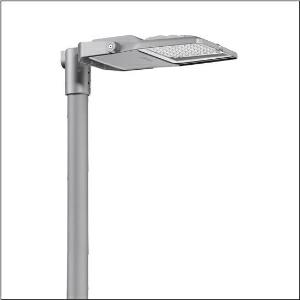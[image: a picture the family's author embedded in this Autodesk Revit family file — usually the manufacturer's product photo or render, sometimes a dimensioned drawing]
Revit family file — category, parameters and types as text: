
# Revit family: floodlight_fl_21_iq_mini___pl33t_5xa7772d4f3a_7ca2
name_source: partatom
category: Lighting Fixtures
units: mm (PartAtom-declared; Revit-internal decimal feet)

## family parameters
Cut with Voids When Loaded = No
Host = Face
Light Source = No
Part Type = Normal
Room Calculation Point = No
Round Connector Dimension = Use Diameter
Shared = No

## types (1)
- --- (1 x LED, 18390 lm, 143 W, 4000K)
    Apparent Load = 143 VA
    CIE Flux Codes = 26 75 99 100 100
    Color Rendering = 70
    Color Temperature = 4000K
    Default Elevation = 1800 mm
    Description = Floodlight FL 21 iQ mini, floodlight, primary light control with lens, of PMMA, primary optical cover: protective disc, of toughened safety glass, transparent, light distribution: PL33T, light emission: direct distribution, installation type: surface-mounted, LED, High Power LED, rated luminous flux: 18.390lm, luminous efficacy: 129lm/W, light colour: 740, colour temperature: 4000K, control: Auto-Match, Temp-Guard, Night-Set, Smart-Wire, Desk-Remote (wireless, voltage-free reading and setting of iQ features in the workshop via application-optimized NFC function/RFID function), optimised constant luminous flux control (CLO 2.0), Light-Fading, Lumen-Switch, with terminal, 6-pole, mains connection: 220..240V, AC, 50/60Hz, start of lifetime: 143W, end of service life: 152W, reduction: 61W, luminaire housing, of diecast aluminium, powder-coated, Siteco® metallic grey (DB 702S), corrosivity category C5 mid according to DIN EN ISO 12944, sealing non-destructively replaceable, please order mast flange separately, mast bracket, of steel, galvanised, powder-coated, protection rating (complete): IP66, insulation class (complete): insulation class II (safety insulation), certification: CE, ENEC, VDE, protection symbol: D, impact resistance: IK08, permissible operating ambient temperature: -40..+40°C, permissible operating ambient temperature for outdoor applications: -40..+50°C, standard: DIN EN 12944, LABS conformity tested according to VDMA 24364:2018-05, packaging unit: 1 piece

Light Distribution: PL33T
    Height = 70 mm
    Lamp = 1 x LED
    Lamp Light Flux = 18390 lm
    Lamp Power = 143 W
    Lamp count = 1
    Length = 485 mm
    Luminous efficacy = 129 lm/W
    Manufacturer = Siteco
    ModVariant = No
    Model = 5XA7772D4F3A
    Number of Poles = 1
    OnlyDefault = Yes
    Power Factor = 1
    Product Name = Floodlight FL 21 iQ mini | PL33T
    Product group = floodlight | pylon annexe
    ProductGroupID = 6200
    Protection Class = Protection class II
    Protection Degree = IP 66
    RLX_Detail_Level = 1
    RLX_Emergency_Light_Flux = 0 lm
    RLX_Emergency_Type = 0
    RLX_Emergency_Type_DB = No
    RlxData = <blob elided: 101605 chars, md5=edd52d3b>
    Socket = socket
    Standby Power = 0 W
    System Light Flux = 18390 lm
    System Power = 143 W
    Type Comments = factory setting: luminous flux: 100 % | dim-lin: 254 | 730 mA
    Type Image = l_1007125.jpg
    URL = http://relux.com
    VarID = @adj_098937
    Voltage = 0 V
    Weight = 0.00 kg
    Width = 337 mm

## geometry (parser evidence)
native form markers: Blend x4, Sweep x12
no freeform markers — native parametric forms only
